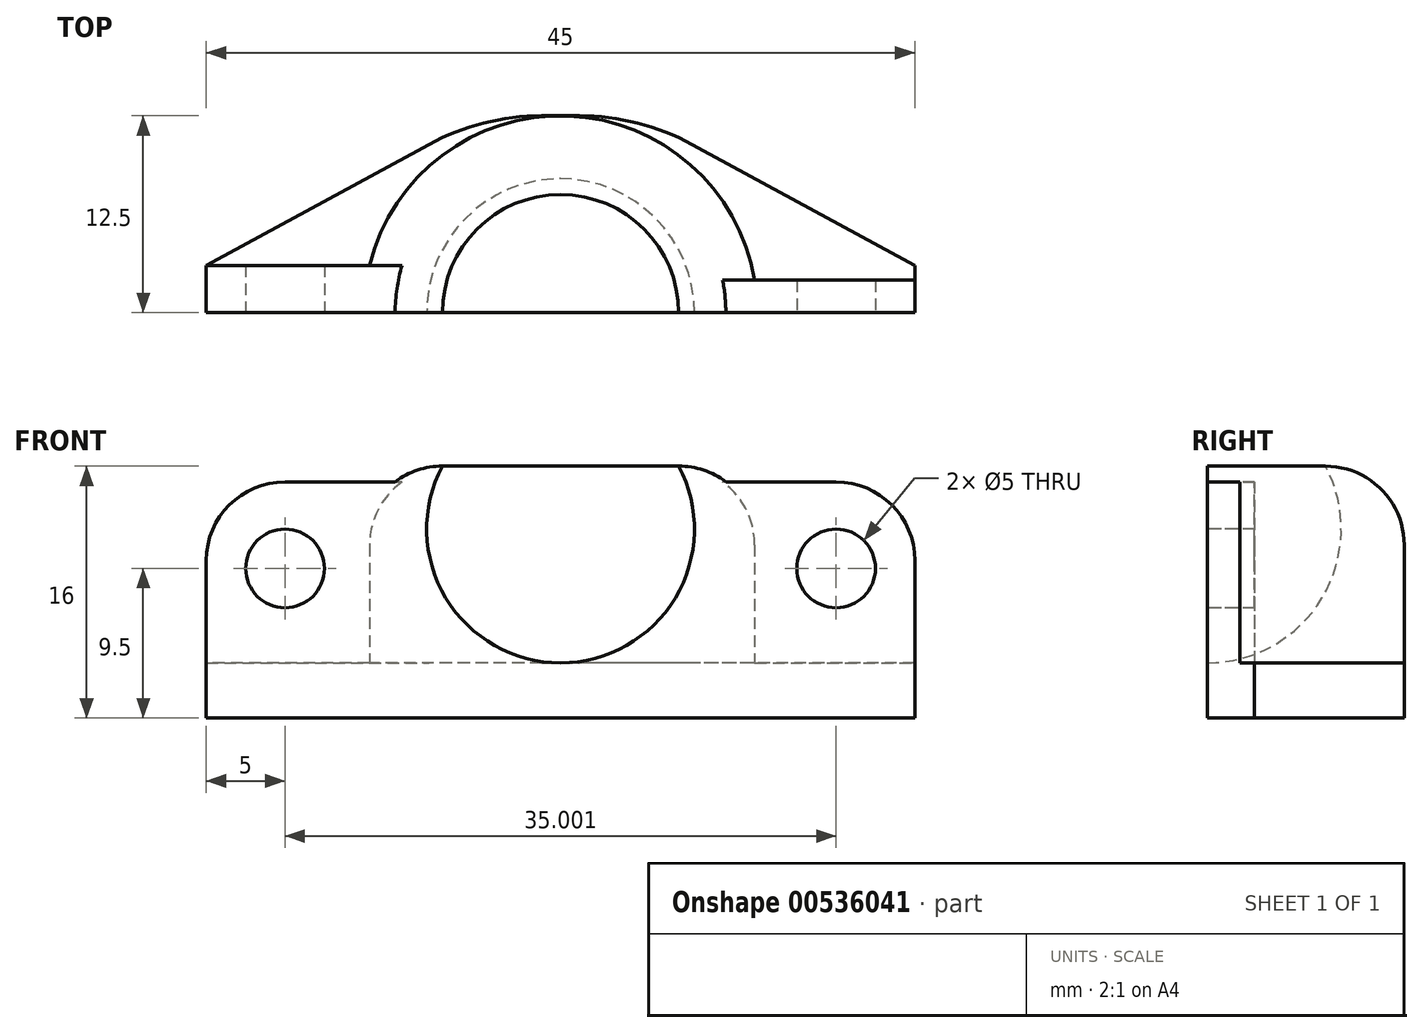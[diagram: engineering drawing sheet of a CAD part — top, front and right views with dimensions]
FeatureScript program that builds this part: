
annotation { "Feature Type Name" : "Feature", "Feature Type Description" : "" }
export const myFeature = defineFeature(function(context is Context, id is Id, definition is map)
    precondition{}
    {
        {
            var Q0;
            Q0=qCreatedBy(makeId("Right.planeOp"),FACE);
            var sketch = newSketch(context, id + "F0", { "sketchPlane" : qUnion([Q0]), "disableImprinting" : false});
            skLineSegment(sketch, "E0", {"start": v(0, 3.5) * mm, "end": v(0, 0) * mm});
            skLineSegment(sketch, "E1", {"start": v(-12.5, 12) * mm, "end": v(-12.5, 0) * mm});
            skLineSegment(sketch, "E2", {"start": v(-12.5, 0) * mm, "end": v(0, 0) * mm});
            skArc(sketch, "E3", {"start": v(-7.5, 16) * mm, "mid": v(-7.29, 7.63) * mm, "end": v(0, 3.5) * mm});
            skLineSegment(sketch, "E4", {"start": v(-11.84, 16) * mm, "end": v(-7.5, 16) * mm});
            skArc(sketch, "E5", {"start": v(-11.84, 16) * mm, "mid": v(-12.33, 14.03) * mm, "end": v(-12.5, 12) * mm});
            skLineSegment(sketch, "E6", {"start": v(0, 0) * mm, "end": v(0, 19.6) * mm});
            skSolve(sketch);
        }
        {
            var Q0;
            Q0=makeQuery(id+"F0.imprint","IMPRINT",FACE,{"disambiguationData":[TD([[makeQuery(id+"F0.imprint","IMPRINT",EDGE,{"derivedFrom":sQuery(id+"F0.wireOp",EDGE,"38JgYKr9-vYyi-n07v-T34V-vSgmsJALgQRt")}),1.0]])]});
            var Q1;
            Q1=makeQuery(id+"F0.imprint","IMPRINT",FACE,{"disambiguationData":[TD([[makeQuery(id+"F0.imprint","IMPRINT",EDGE,{"derivedFrom":sQuery(id+"F0.wireOp",EDGE,"E1")}),1.0]])]});
            var Q2;
            Q2=sQuery(id+"F0.wireOp",EDGE,"E6");
            revolve(context, id + "F1", {"surfaceOperationType" : NewSurfaceOperationType.NEW, "entities" : qUnion([Q0, Q1]), "axis" : qUnion([Q2]), "revolveType" : RevolveType.FULL});
        }
        {
            var Q0;
            Q0=qCreatedBy(makeId("Top.planeOp"),FACE);
            var sketch = newSketch(context, id + "F2", { "sketchPlane" : qUnion([Q0])});
            skLineSegment(sketch, "E7.bottom", {"start": v(-5, -12.5) * mm, "end": v(5, -12.5) * mm});
            skLineSegment(sketch, "E7.top", {"start": v(-5, 12.5) * mm, "end": v(5, 12.5) * mm});
            skLineSegment(sketch, "E7.left", {"start": v(-22.5, -3) * mm, "end": v(-22.5, 3) * mm});
            skLineSegment(sketch, "E7.right", {"start": v(22.5, -3) * mm, "end": v(22.5, 3) * mm});
            skLineSegment(sketch, "E8", {"start": v(22.5, 3) * mm, "end": v(22.5, 0) * mm});
            skLineSegment(sketch, "E9", {"start": v(-22.5, 3) * mm, "end": v(-22.5, 0) * mm});
            skLineSegment(sketch, "E10", {"start": v(-22.5, 3) * mm, "end": v(-5, 12.5) * mm});
            skLineSegment(sketch, "E11", {"start": v(22.5, 3) * mm, "end": v(5, 12.5) * mm});
            skLineSegment(sketch, "E12", {"start": v(-22.5, -3) * mm, "end": v(-5, -12.5) * mm});
            skLineSegment(sketch, "E13", {"start": v(22.5, -3) * mm, "end": v(5, -12.5) * mm});
            skPoint(sketch, "E14.end.orphan", {"position": v(0, 12.5) * mm});
            skPoint(sketch, "E15.orphan", {"position": v(-22.5, 12.5) * mm});
            skPoint(sketch, "E16.orphan", {"position": v(-22.5, -12.5) * mm});
            skSolve(sketch);
        }
        {
            var Q0;
            Q0 = qSketchRegion(id + "F2", true);
            var Q1;
            Q1=makeQuery(id+"F2.imprint","IMPRINT",FACE,{"disambiguationData":[TD([[makeQuery(id+"F2.imprint","IMPRINT",EDGE,{"derivedFrom":sQuery(id+"F2.wireOp",EDGE,"E7.bottom")}),1.0]])]});
            extrude(context, id + "F3", {"entities" : qUnion([Q0, Q1]), "operationType" : NewBodyOperationType.ADD, "depth" : 3.5 * mm, "offsetDistance" : 25 * mm});
        }
        {
            var Q0;
            Q0=qCreatedBy(makeId("Top.planeOp"),FACE);
            var sketch = newSketch(context, id + "F4", { "sketchPlane" : qUnion([Q0])});
            skLineSegment(sketch, "E17.bottom", {"start": v(-22.5, 0) * mm, "end": v(-10.67, 0) * mm});
            skLineSegment(sketch, "E17.top", {"start": v(-22.5, 3) * mm, "end": v(-10.67, 3) * mm});
            skLineSegment(sketch, "E17.left", {"start": v(-22.5, 0) * mm, "end": v(-22.5, 3) * mm});
            skLineSegment(sketch, "E17.right", {"start": v(-10.67, 0) * mm, "end": v(-10.67, 3) * mm});
            skLineSegment(sketch, "E18.bottom", {"start": v(-22.5, 0) * mm, "end": v(-10.63, 0) * mm});
            skLineSegment(sketch, "E18.top", {"start": v(-22.5, -3) * mm, "end": v(-10.63, -3) * mm});
            skLineSegment(sketch, "E18.left", {"start": v(-22.5, 0) * mm, "end": v(-22.5, -3) * mm});
            skLineSegment(sketch, "E18.right", {"start": v(-10.63, 0) * mm, "end": v(-10.63, -3) * mm});
            skLineSegment(sketch, "E19.bottom", {"start": v(22.5, 0) * mm, "end": v(11, 0) * mm});
            skLineSegment(sketch, "E19.top", {"start": v(22.5, -3) * mm, "end": v(11, -3) * mm});
            skLineSegment(sketch, "E19.left", {"start": v(22.5, 0) * mm, "end": v(22.5, -3) * mm});
            skLineSegment(sketch, "E19.right", {"start": v(11, 0) * mm, "end": v(11, -3) * mm});
            skLineSegment(sketch, "E20.bottom", {"start": v(22.5, 0) * mm, "end": v(11.02, 0) * mm});
            skLineSegment(sketch, "E20.top", {"start": v(22.5, 2.06) * mm, "end": v(11.02, 2.06) * mm});
            skLineSegment(sketch, "E20.left", {"start": v(22.5, 0) * mm, "end": v(22.5, 2.06) * mm});
            skLineSegment(sketch, "E20.right", {"start": v(11.02, 0) * mm, "end": v(11.02, 2.06) * mm});
            skSolve(sketch);
        }
        {
            var Q0;
            Q0 = qSketchRegion(id + "F4", true);
            extrude(context, id + "F5", {"entities" : qUnion([Q0]), "operationType" : NewBodyOperationType.ADD, "depth" : 15 * mm, "offsetDistance" : 25 * mm});
        }
        {
            var Q0;
            Q0=makeQuery(id+"F5.opExtrude","CAP_EDGE",EDGE,{"disambiguationData":[OSD([sQuery(id+"F4.wireOp",EDGE,"E17.left"),sQuery(id+"F4.wireOp",EDGE,"E18.left")])],"isStart":false});
            var Q1;
            Q1=makeQuery(id+"F5.opExtrude","CAP_EDGE",EDGE,{"disambiguationData":[OSD([sQuery(id+"F4.wireOp",EDGE,"E19.left"),sQuery(id+"F4.wireOp",EDGE,"E20.left")])],"isStart":false});
            fillet(context, id + "F6", {"entities" : qUnion([Q0, Q1]), "radius" : 5 * mm, "tangentPropagation" : true, "allowEdgeOverflow" : false});
        }
        {
            var Q0;
            Q0=makeQuery(id+"F3.opExtrude","SWEPT_EDGE",EDGE,{"disambiguationData":[OSD([sQuery(id+"F2.wireOp",EDGE,"E7.bottom"),sQuery(id+"F2.wireOp",EDGE,"E12")])]});
            var Q1;
            Q1=makeQuery(id+"F3.opExtrude","SWEPT_EDGE",EDGE,{"disambiguationData":[OSD([sQuery(id+"F2.wireOp",EDGE,"E7.bottom"),sQuery(id+"F2.wireOp",EDGE,"E13")])]});
            fillet(context, id + "F7", {"entities" : qUnion([Q0, Q1]), "radius" : 5 * mm, "tangentPropagation" : true, "allowEdgeOverflow" : false});
        }
        {
            var Q0;
            Q0=makeQuery(id+"F3.opExtrude","SWEPT_EDGE",EDGE,{"disambiguationData":[OSD([sQuery(id+"F2.wireOp",EDGE,"E7.top"),sQuery(id+"F2.wireOp",EDGE,"E10")])]});
            var Q1;
            Q1=makeQuery(id+"F3.opExtrude","SWEPT_EDGE",EDGE,{"disambiguationData":[OSD([sQuery(id+"F2.wireOp",EDGE,"E7.top"),sQuery(id+"F2.wireOp",EDGE,"E11")])]});
            fillet(context, id + "F8", {"entities" : qUnion([Q0, Q1]), "radius" : 15 * mm, "tangentPropagation" : true, "allowEdgeOverflow" : false});
        }
        {
            var Q0;
            Q0=makeQuery(id+"F5.opExtrude","SWEPT_FACE",FACE,{"disambiguationData":[OSD([sQuery(id+"F4.wireOp",EDGE,"E18.top")])]});
            var sketch = newSketch(context, id + "F9", { "sketchPlane" : qUnion([Q0])});
            skCircle(sketch, "E21", {"center": v(-17.5, 9.5) * mm, "radius": 2.5 * mm});
            skSolve(sketch);
        }
        {
            var Q0;
            Q0 = qSketchRegion(id + "F9", true);
            extrude(context, id + "F10", {"entities" : qUnion([Q0]), "operationType" : NewBodyOperationType.REMOVE, "oppositeDirection" : true, "depth" : 25 * mm, "offsetDistance" : 25 * mm, "symmetric" : true});
        }
        {
            var Q0;
            Q0=makeQuery(id+"F5.opExtrude","SWEPT_FACE",FACE,{"disambiguationData":[OSD([sQuery(id+"F4.wireOp",EDGE,"E19.top")])]});
            var sketch = newSketch(context, id + "F11", { "sketchPlane" : qUnion([Q0])});
            skCircle(sketch, "E22", {"center": v(17.5, 9.5) * mm, "radius": 2.5 * mm});
            skSolve(sketch);
        }
        {
            var Q0;
            Q0 = qSketchRegion(id + "F11", true);
            extrude(context, id + "F12", {"entities" : qUnion([Q0]), "operationType" : NewBodyOperationType.REMOVE, "oppositeDirection" : true, "depth" : 25 * mm, "offsetDistance" : 25 * mm, "symmetric" : true});
        }
        {
            var Q0;
            Q0=qCreatedBy(makeId("Front.planeOp"),FACE);
            var sketch = newSketch(context, id + "F13", { "sketchPlane" : qUnion([Q0])});
            skLineSegment(sketch, "E23.bottom", {"start": v(-35.26, 31.44) * mm, "end": v(36.17, 31.44) * mm});
            skLineSegment(sketch, "E23.top", {"start": v(-35.26, 0) * mm, "end": v(36.17, 0) * mm});
            skLineSegment(sketch, "E23.left", {"start": v(-35.26, 31.44) * mm, "end": v(-35.26, 0) * mm});
            skLineSegment(sketch, "E23.right", {"start": v(36.17, 31.44) * mm, "end": v(36.17, 0) * mm});
            skSolve(sketch);
        }
        {
            var Q0;
            Q0 = qSketchRegion(id + "F13", true);
            extrude(context, id + "F14", {"entities" : qUnion([Q0]), "operationType" : NewBodyOperationType.REMOVE, "depth" : 25 * mm, "offsetDistance" : 25 * mm});
        }
        {
            var Q0;
            Q0=makeQuery(id+"F1.opRevolve","SWEPT_EDGE",EDGE,{"disambiguationData":[OSD([sQuery(id+"F0.wireOp",EDGE,"E4"),sQuery(id+"F0.wireOp",EDGE,"E5")])]});
            fillet(context, id + "F15", {"entities" : qUnion([Q0]), "radius" : 5 * mm, "tangentPropagation" : true, "allowEdgeOverflow" : false});
        }
    });
